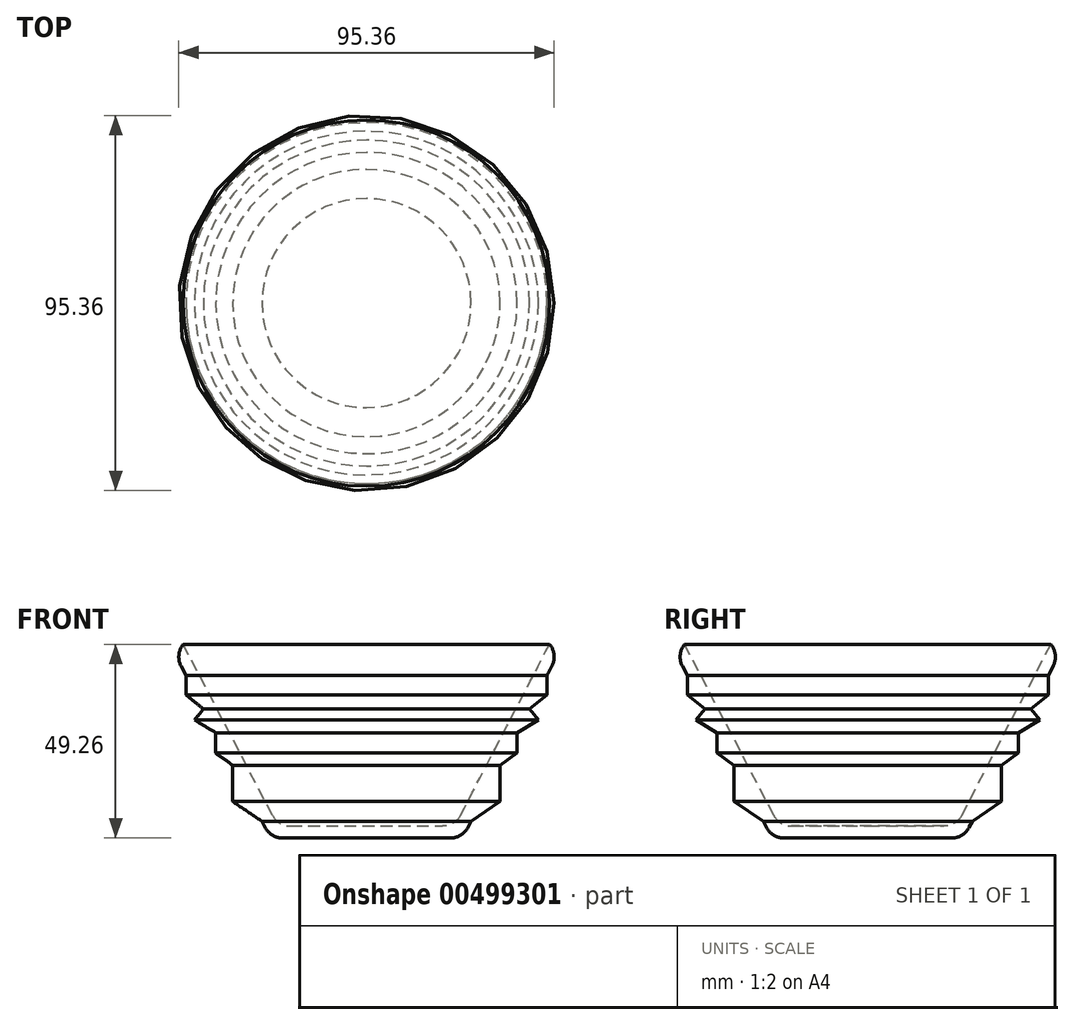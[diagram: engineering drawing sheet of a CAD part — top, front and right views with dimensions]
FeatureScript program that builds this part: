
annotation { "Feature Type Name" : "Feature", "Feature Type Description" : "" }
export const myFeature = defineFeature(function(context is Context, id is Id, definition is map)
    precondition{}
    {
        {
            var Q0;
            Q0=qCreatedBy(makeId("Front.planeOp"),FACE);
            var sketch = newSketch(context, id + "F0", { "sketchPlane" : qUnion([Q0])});
            skLineSegment(sketch, "E0", {"start": v(0, 0) * mm, "end": v(0, 50.8) * mm, "construction": true});
            skLineSegment(sketch, "E1", {"start": v(0, 0) * mm, "end": v(24.33, 0) * mm});
            skLineSegment(sketch, "E2", {"start": v(24.33, 0) * mm, "end": v(50.8, 50.8) * mm});
            skLineSegment(sketch, "E3.0", {"start": v(22.47, 3.07) * mm, "end": v(46.53, 49.26) * mm});
            skLineSegment(sketch, "E3.1", {"start": v(0, 3.07) * mm, "end": v(22.47, 3.07) * mm});
            skLineSegment(sketch, "E4", {"start": v(50.8, 50.8) * mm, "end": v(46.53, 49.26) * mm});
            skLineSegment(sketch, "E5", {"start": v(0, 3.07) * mm, "end": v(0, 0) * mm});
            skLineSegment(sketch, "E6", {"start": v(45.86, 41.32) * mm, "end": v(45.86, 36.44) * mm});
            skLineSegment(sketch, "E7", {"start": v(45.86, 36.44) * mm, "end": v(41.41, 32.79) * mm});
            skLineSegment(sketch, "E8", {"start": v(41.41, 32.79) * mm, "end": v(43.68, 30.03) * mm});
            skLineSegment(sketch, "E9", {"start": v(43.68, 30.03) * mm, "end": v(38.28, 26.77) * mm});
            skLineSegment(sketch, "E10", {"start": v(38.28, 26.77) * mm, "end": v(38.28, 21.59) * mm});
            skLineSegment(sketch, "E11", {"start": v(38.28, 21.59) * mm, "end": v(33.98, 18.51) * mm});
            skLineSegment(sketch, "E12", {"start": v(33.98, 18.51) * mm, "end": v(33.98, 10.6) * mm});
            skLineSegment(sketch, "E13", {"start": v(33.98, 9.3) * mm, "end": v(26.56, 4.28) * mm});
            skLineSegment(sketch, "E14", {"start": v(33.98, 9.3) * mm, "end": v(33.98, 10.6) * mm});
            skSolve(sketch);
        }
        {
            var Q0;
            Q0=makeQuery(id+"F0.imprint","IMPRINT",FACE,{"disambiguationData":[TD([[makeQuery(id+"F0.imprint","IMPRINT",EDGE,{"derivedFrom":sQuery(id+"F0.wireOp",EDGE,"E1")}),1.0]])]});
            var Q1;
            {var subQ0=sQuery(id+"F0.wireOp",EDGE,"E6");Q1=makeQuery(id+"F0.imprint","IMPRINT",FACE,{"disambiguationData":[TD([[makeQuery(id+"F0.imprint","IMPRINT",EDGE,{"derivedFrom":subQ0}),-1.0]])]});}
            var Q2;
            {var subQ0=sQuery(id+"F0.wireOp",EDGE,"E8");Q2=makeQuery(id+"F0.imprint","IMPRINT",FACE,{"disambiguationData":[TD([[makeQuery(id+"F0.imprint","IMPRINT",EDGE,{"derivedFrom":subQ0}),-1.0]])]});}
            var Q3;
            {var subQ0=sQuery(id+"F0.wireOp",EDGE,"E10");Q3=makeQuery(id+"F0.imprint","IMPRINT",FACE,{"disambiguationData":[TD([[makeQuery(id+"F0.imprint","IMPRINT",EDGE,{"derivedFrom":subQ0}),-1.0]])]});}
            var Q4;
            {var subQ0=sQuery(id+"F0.wireOp",EDGE,"E12");Q4=makeQuery(id+"F0.imprint","IMPRINT",FACE,{"disambiguationData":[TD([[makeQuery(id+"F0.imprint","IMPRINT",EDGE,{"derivedFrom":subQ0}),-1.0]])]});}
            var Q5;
            Q5=sQuery(id+"F0.wireOp",EDGE,"E0");
            revolve(context, id + "F1", {"entities" : qUnion([Q0, Q1, Q2, Q3, Q4]), "axis" : qUnion([Q5]), "revolveType" : RevolveType.FULL});
        }
        {
            var Q0;
            Q0=makeQuery(id+"F1.opRevolve","SWEPT_EDGE",EDGE,{"disambiguationData":[OSD([sQuery(id+"F0.wireOp",EDGE,"E2"),sQuery(id+"F0.wireOp",EDGE,"E4")])]});
            fillet(context, id + "F2", {"entities" : qUnion([Q0]), "radius" : 5.08 * mm, "tangentPropagation" : true, "allowEdgeOverflow" : false});
        }
        {
            var Q0;
            Q0=makeQuery(id+"F1.opRevolve","SWEPT_EDGE",EDGE,{"disambiguationData":[OSD([sQuery(id+"F0.wireOp",EDGE,"E1"),sQuery(id+"F0.wireOp",EDGE,"E2")])]});
            fillet(context, id + "F3", {"entities" : qUnion([Q0]), "radius" : 5.08 * mm, "tangentPropagation" : true, "allowEdgeOverflow" : false});
        }
        {
            var Q0;
            Q0=makeQuery(id+"F1.opRevolve","SWEPT_EDGE",EDGE,{"disambiguationData":[OSD([sQuery(id+"F0.wireOp",EDGE,"E3.0"),sQuery(id+"F0.wireOp",EDGE,"E3.1")])]});
            fillet(context, id + "F4", {"entities" : qUnion([Q0]), "radius" : 5.08 * mm, "tangentPropagation" : true, "allowEdgeOverflow" : false});
        }
    });
